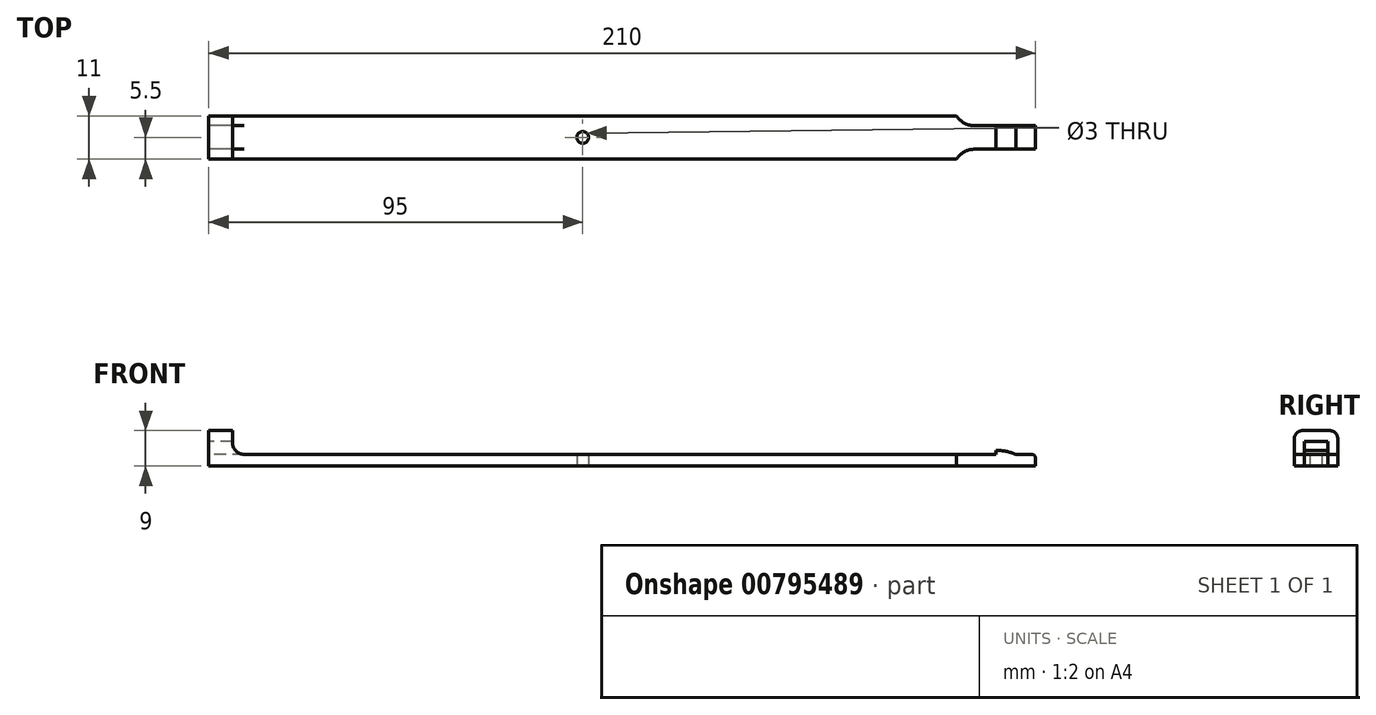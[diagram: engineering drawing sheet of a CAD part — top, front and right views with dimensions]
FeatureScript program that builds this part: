
annotation { "Feature Type Name" : "Feature", "Feature Type Description" : "" }
export const myFeature = defineFeature(function(context is Context, id is Id, definition is map)
    precondition{}
    {
        {
            var Q0;
            Q0=qCreatedBy(makeId("Top.planeOp"),FACE);
            var sketch = newSketch(context, id + "F0", { "sketchPlane" : qUnion([Q0])});
            skLineSegment(sketch, "E0.bottom", {"start": v(95, -5.5) * mm, "end": v(-95, -5.5) * mm});
            skLineSegment(sketch, "E0.top", {"start": v(95, 5.5) * mm, "end": v(-95, 5.5) * mm});
            skLineSegment(sketch, "E0.left", {"start": v(95, -5.5) * mm, "end": v(95, -3) * mm});
            skLineSegment(sketch, "E0.right", {"start": v(-95, -5.5) * mm, "end": v(-95, 5.5) * mm});
            skPoint(sketch, "E0.middle", {"position": v(0, 0) * mm});
            skPoint(sketch, "E1.cornerSnap0", {"position": v(95, 0) * mm});
            skLineSegment(sketch, "E2.bottom", {"start": v(115, -3) * mm, "end": v(95, -3) * mm});
            skLineSegment(sketch, "E2.top", {"start": v(115, 3) * mm, "end": v(95, 3) * mm});
            skLineSegment(sketch, "E2.left", {"start": v(115, -3) * mm, "end": v(115, 3) * mm});
            skLineSegment(sketch, "E3.trimOffspring", {"start": v(95, 3) * mm, "end": v(95, 5.5) * mm});
            skLineSegment(sketch, "E4", {"start": v(-89, 5.5) * mm, "end": v(-89, -5.5) * mm});
            skCircle(sketch, "E5", {"center": v(0, 0) * mm, "radius": 1.5 * mm});
            skSolve(sketch);
        }
        {
            var Q0;
            {var subQ0=sQuery(id+"F0.wireOp",EDGE,"E0.right");Q0=makeQuery(id+"F0.imprint","IMPRINT",FACE,{"disambiguationData":[TD([[makeQuery(id+"F0.imprint","IMPRINT",EDGE,{"derivedFrom":subQ0}),-1.0]])]});}
            var Q1;
            {var subQ0=sQuery(id+"F0.wireOp",EDGE,"E0.left");Q1=makeQuery(id+"F0.imprint","IMPRINT",FACE,{"disambiguationData":[TD([[makeQuery(id+"F0.imprint","IMPRINT",EDGE,{"derivedFrom":subQ0}),1.0]])]});}
            extrude(context, id + "F1", {"entities" : qUnion([Q0, Q1]), "depth" : 3 * mm, "offsetDistance" : 25 * mm});
        }
        {
            var Q0;
            {var subQ0=sQuery(id+"F0.wireOp",EDGE,"E0.right");Q0=makeQuery(id+"F0.imprint","IMPRINT",FACE,{"disambiguationData":[TD([[makeQuery(id+"F0.imprint","IMPRINT",EDGE,{"derivedFrom":subQ0}),-1.0]])]});}
            extrude(context, id + "F2", {"entities" : qUnion([Q0]), "operationType" : NewBodyOperationType.ADD, "depth" : 9 * mm, "offsetDistance" : 25 * mm});
        }
        {
            var Q0;
            {var subQ0=sQuery(id+"F0.wireOp",EDGE,"E0.right");Q0=makeQuery(id+"F2.boolean.opBoolean","MERGE",FACE,{"derivedFrom":[makeQuery(id+"F1.opExtrude","SWEPT_FACE",FACE,{"disambiguationData":[OSD([subQ0])]}),makeQuery(id+"F2.opExtrude","SWEPT_FACE",FACE,{"disambiguationData":[OSD([subQ0])]})]});}
            var sketch = newSketch(context, id + "F3", { "sketchPlane" : qUnion([Q0])});
            skLineSegment(sketch, "E6", {"start": v(-9.62, 3) * mm, "end": v(12, 3) * mm, "construction": true});
            skLineSegment(sketch, "E7", {"start": v(-9.62, 6.2) * mm, "end": v(12.59, 6.2) * mm, "construction": true});
            skLineSegment(sketch, "E8", {"start": v(-3, 12.6) * mm, "end": v(-3, -5.02) * mm, "construction": true});
            skLineSegment(sketch, "E9", {"start": v(3, 12.81) * mm, "end": v(3, -5.52) * mm, "construction": true});
            skLineSegment(sketch, "E10", {"start": v(-3, 6.2) * mm, "end": v(3, 6.2) * mm});
            skLineSegment(sketch, "E11", {"start": v(3, 6.2) * mm, "end": v(3, 3) * mm});
            skLineSegment(sketch, "E12", {"start": v(3, 3) * mm, "end": v(-3, 3) * mm});
            skLineSegment(sketch, "E13", {"start": v(-3, 3) * mm, "end": v(-3, 6.2) * mm});
            skSolve(sketch);
        }
        {
            var Q0;
            Q0=makeQuery(id+"F3.imprint","IMPRINT",FACE,{"disambiguationData":[TD([[makeQuery(id+"F3.imprint","IMPRINT",EDGE,{"derivedFrom":sQuery(id+"F3.wireOp",EDGE,"E10")}),-1.0]])]});
            extrude(context, id + "F4", {"entities" : qUnion([Q0]), "operationType" : NewBodyOperationType.REMOVE, "endBound" : BoundingType.SYMMETRIC, "oppositeDirection" : true, "depth" : 30 * mm, "offsetDistance" : 25 * mm});
        }
        {
            var Q0;
            Q0=makeQuery(id+"F4.boolean.opBoolean","MERGE",FACE,{"derivedFrom":[makeQuery(id+"F1.opExtrude","CAP_FACE",FACE,{"disambiguationData":[OSD([sQuery(id+"F0.wireOp",EDGE,"E0.bottom"),sQuery(id+"F0.wireOp",EDGE,"E0.top"),sQuery(id+"F0.wireOp",EDGE,"E0.left"),sQuery(id+"F0.wireOp",EDGE,"E0.right"),sQuery(id+"F0.wireOp",EDGE,"E2.bottom"),sQuery(id+"F0.wireOp",EDGE,"E2.top"),sQuery(id+"F0.wireOp",EDGE,"E2.left"),sQuery(id+"F0.wireOp",EDGE,"E3.trimOffspring")])],"isStart":false}),makeQuery(id+"F4.opExtrude","SWEPT_FACE",FACE,{"disambiguationData":[OSD([sQuery(id+"F3.wireOp",EDGE,"E12")])]})]});
            var sketch = newSketch(context, id + "F5", { "sketchPlane" : qUnion([Q0])});
            skLineSegment(sketch, "E14", {"start": v(110, 3) * mm, "end": v(110, -3) * mm});
            skLineSegment(sketch, "E15", {"start": v(105, 3) * mm, "end": v(105, -3) * mm});
            skSolve(sketch);
        }
        {
            var Q0;
            {var subQ0=sQuery(id+"F5.wireOp",EDGE,"E14");Q0=makeQuery(id+"F5.imprint","IMPRINT",FACE,{"disambiguationData":[TD([[makeQuery(id+"F5.imprint","IMPRINT",EDGE,{"derivedFrom":subQ0}),-1.0]])]});}
            extrude(context, id + "F6", {"entities" : qUnion([Q0]), "operationType" : NewBodyOperationType.ADD, "depth" : 1 * mm, "offsetDistance" : 25 * mm});
        }
        {
            var Q0;
            Q0=makeQuery(id+"F6.opExtrude","CAP_EDGE",EDGE,{"disambiguationData":[OSD([sQuery(id+"F5.wireOp",EDGE,"E14")])],"isStart":false});
            fillet(context, id + "F7", {"entities" : qUnion([Q0]), "radius" : 13 * mm, "tangentPropagation" : true, "allowEdgeOverflow" : false});
        }
        {
            var Q0;
            {var subQ0=makeQuery(id+"F2.opExtrude","SWEPT_FACE",FACE,{"disambiguationData":[OSD([sQuery(id+"F0.wireOp",EDGE,"E4")])]});var subQ1=sQuery(id+"F0.wireOp",EDGE,"E0.bottom");var subQ2=makeQuery(id+"F1.opExtrude","CAP_FACE",FACE,{"disambiguationData":[OSD([subQ1,sQuery(id+"F0.wireOp",EDGE,"E0.top"),sQuery(id+"F0.wireOp",EDGE,"E0.left"),sQuery(id+"F0.wireOp",EDGE,"E0.right"),sQuery(id+"F0.wireOp",EDGE,"E2.bottom"),sQuery(id+"F0.wireOp",EDGE,"E2.top"),sQuery(id+"F0.wireOp",EDGE,"E2.left"),sQuery(id+"F0.wireOp",EDGE,"E3.trimOffspring")])],"isStart":false});Q0=makeQuery(id+"F4.boolean.opBoolean","SPLIT",EDGE,{"disambiguationData":[TD([makeQuery(id+"F1.opExtrude","SWEPT_FACE",FACE,{"disambiguationData":[OSD([subQ1])]})])],"derivedFrom":makeQuery(id+"F2.boolean.opBoolean","INTERSECT",EDGE,{"derivedFrom":[subQ2,subQ0]})});}
            var Q1;
            {var subQ0=makeQuery(id+"F2.opExtrude","SWEPT_FACE",FACE,{"disambiguationData":[OSD([sQuery(id+"F0.wireOp",EDGE,"E4")])]});var subQ1=sQuery(id+"F0.wireOp",EDGE,"E0.top");var subQ2=makeQuery(id+"F1.opExtrude","CAP_FACE",FACE,{"disambiguationData":[OSD([sQuery(id+"F0.wireOp",EDGE,"E0.bottom"),subQ1,sQuery(id+"F0.wireOp",EDGE,"E0.left"),sQuery(id+"F0.wireOp",EDGE,"E0.right"),sQuery(id+"F0.wireOp",EDGE,"E2.bottom"),sQuery(id+"F0.wireOp",EDGE,"E2.top"),sQuery(id+"F0.wireOp",EDGE,"E2.left"),sQuery(id+"F0.wireOp",EDGE,"E3.trimOffspring")])],"isStart":false});Q1=makeQuery(id+"F4.boolean.opBoolean","SPLIT",EDGE,{"disambiguationData":[TD([makeQuery(id+"F1.opExtrude","SWEPT_FACE",FACE,{"disambiguationData":[OSD([subQ1])]})])],"derivedFrom":makeQuery(id+"F2.boolean.opBoolean","INTERSECT",EDGE,{"derivedFrom":[subQ2,subQ0]})});}
            fillet(context, id + "F8", {"entities" : qUnion([Q0, Q1]), "radius" : 3 * mm, "tangentPropagation" : true, "allowEdgeOverflow" : false});
        }
        {
            var Q0;
            Q0=makeQuery(id+"F1.opExtrude","CAP_EDGE",EDGE,{"disambiguationData":[OSD([sQuery(id+"F0.wireOp",EDGE,"E2.left")])],"isStart":false});
            fillet(context, id + "F9", {"entities" : qUnion([Q0]), "radius" : 1 * mm, "tangentPropagation" : true, "allowEdgeOverflow" : false});
        }
        {
            var Q0;
            Q0=makeQuery(id+"F1.opExtrude","SWEPT_EDGE",EDGE,{"disambiguationData":[OSD([sQuery(id+"F0.wireOp",EDGE,"E0.left"),sQuery(id+"F0.wireOp",EDGE,"E2.bottom")])]});
            var Q1;
            Q1=makeQuery(id+"F1.opExtrude","SWEPT_EDGE",EDGE,{"disambiguationData":[OSD([sQuery(id+"F0.wireOp",EDGE,"E2.top"),sQuery(id+"F0.wireOp",EDGE,"E3.trimOffspring")])]});
            fillet(context, id + "F10", {"entities" : qUnion([Q0, Q1]), "radius" : 5 * mm, "tangentPropagation" : true, "allowEdgeOverflow" : false});
        }
        {
            var Q0;
            Q0=makeQuery(id+"F2.opExtrude","CAP_EDGE",EDGE,{"disambiguationData":[OSD([sQuery(id+"F0.wireOp",EDGE,"E0.top")])],"isStart":false});
            var Q1;
            Q1=makeQuery(id+"F2.opExtrude","CAP_EDGE",EDGE,{"disambiguationData":[OSD([sQuery(id+"F0.wireOp",EDGE,"E0.bottom")])],"isStart":false});
            fillet(context, id + "F11", {"entities" : qUnion([Q0, Q1]), "radius" : 2 * mm, "tangentPropagation" : true, "allowEdgeOverflow" : false});
        }
    });
